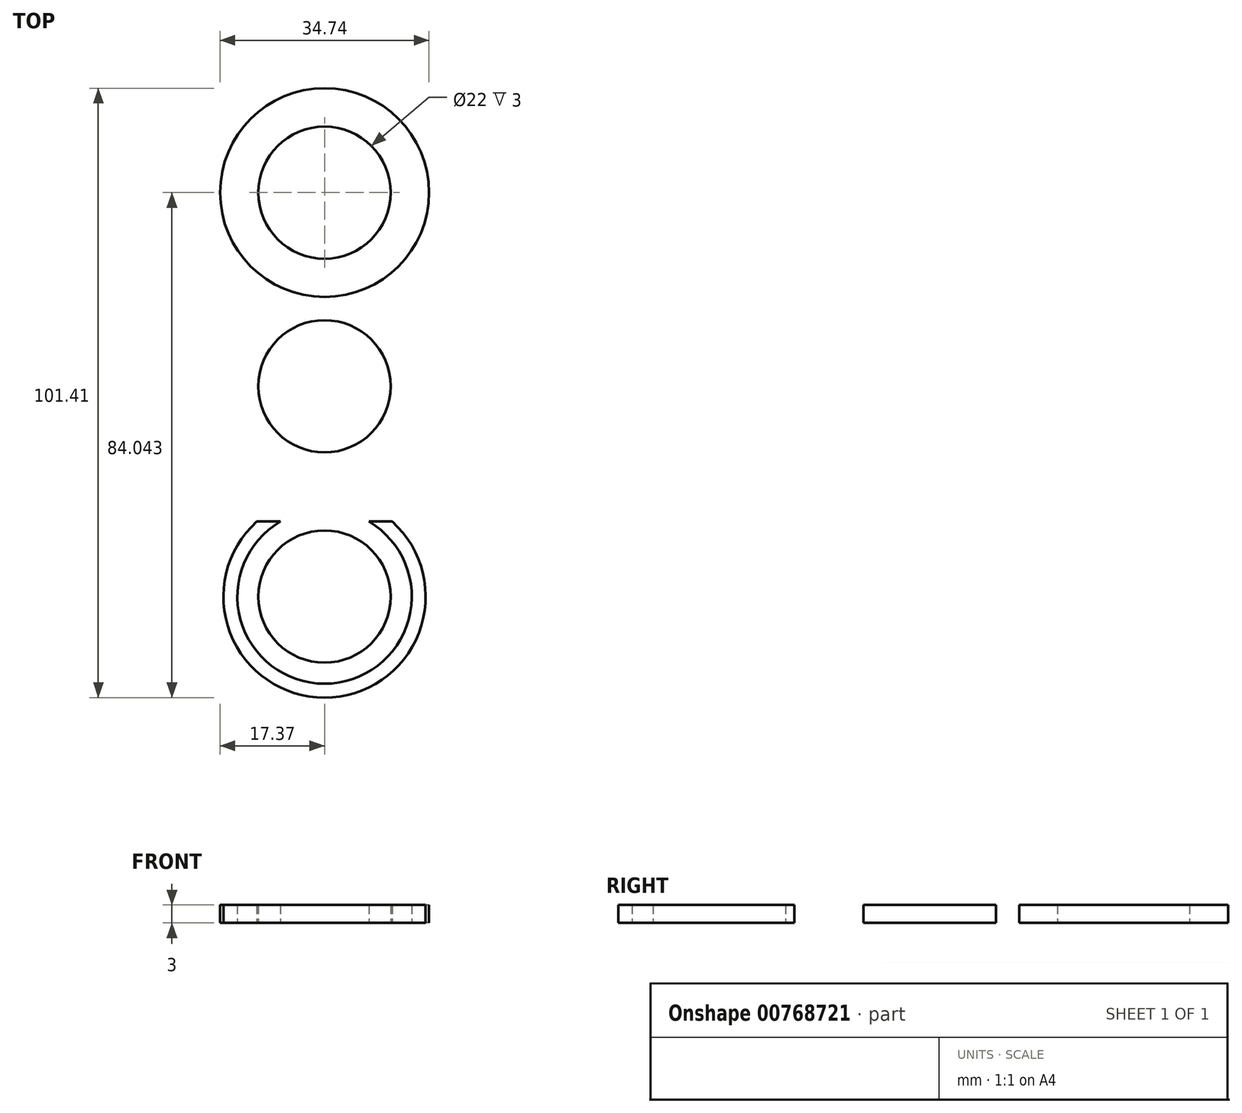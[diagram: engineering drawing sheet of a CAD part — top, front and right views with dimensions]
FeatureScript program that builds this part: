
annotation { "Feature Type Name" : "Feature", "Feature Type Description" : "" }
export const myFeature = defineFeature(function(context is Context, id is Id, definition is map)
    precondition{}
    {
        {
            var Q0;
            Q0=qCreatedBy(makeId("Top.planeOp"),FACE);
            var sketch = newSketch(context, id + "F0", { "sketchPlane" : qUnion([Q0])});
            skArc(sketch, "E0", {"start": v(11, 0) * mm, "mid": v(0, 11) * mm, "end": v(-11, 0) * mm});
            skCircle(sketch, "E1", {"center": v(0, 32.23) * mm, "radius": 11 * mm});
            skArc(sketch, "E2", {"start": v(-6.71, 16.16) * mm, "mid": v(-14.56, 9.71) * mm, "end": v(-17.5, 0) * mm});
            skArc(sketch, "E3.trimOffspring", {"start": v(17.5, 0) * mm, "mid": v(14.56, 9.71) * mm, "end": v(6.71, 16.16) * mm});
            skLineSegment(sketch, "E4.MirrorCS", {"start": v(7.36, -22.5) * mm, "end": v(11.25, -22.5) * mm});
            skLineSegment(sketch, "E5.MirrorCS", {"start": v(-11.25, -22.5) * mm, "end": v(-7.36, -22.5) * mm});
            skArc(sketch, "E6.MirrorCS", {"start": v(11.25, -22.5) * mm, "mid": v(0, -51.81) * mm, "end": v(-11.25, -22.5) * mm});
            skArc(sketch, "E7.MirrorCS", {"start": v(7.36, -22.5) * mm, "mid": v(0, -49.5) * mm, "end": v(-7.36, -22.5) * mm});
            skArc(sketch, "E8.MirrorCS", {"start": v(17.5, 0) * mm, "mid": v(14.56, -9.71) * mm, "end": v(6.71, -16.16) * mm});
            skArc(sketch, "E9.MirrorCS", {"start": v(-6.71, -16.16) * mm, "mid": v(-14.56, -9.71) * mm, "end": v(-17.5, 0) * mm});
            skArc(sketch, "E10.MirrorCS", {"start": v(6.71, -16.16) * mm, "mid": v(0, -55) * mm, "end": v(-6.71, -16.16) * mm});
            skCircle(sketch, "E11.MirrorC", {"center": v(0, -35) * mm, "radius": 11 * mm});
            skArc(sketch, "E12.MirrorCS", {"start": v(11, 0) * mm, "mid": v(0, -11) * mm, "end": v(-11, 0) * mm});
            skCircle(sketch, "E13", {"center": v(0, 32.23) * mm, "radius": 17.37 * mm});
            skSolve(sketch);
        }
        {
            var Q0;
            Q0 = qSketchRegion(id + "F0", true);
            extrude(context, id + "F1", {"entities" : qUnion([Q0]), "depth" : 3 * mm, "offsetDistance" : 25 * mm});
        }
    });
